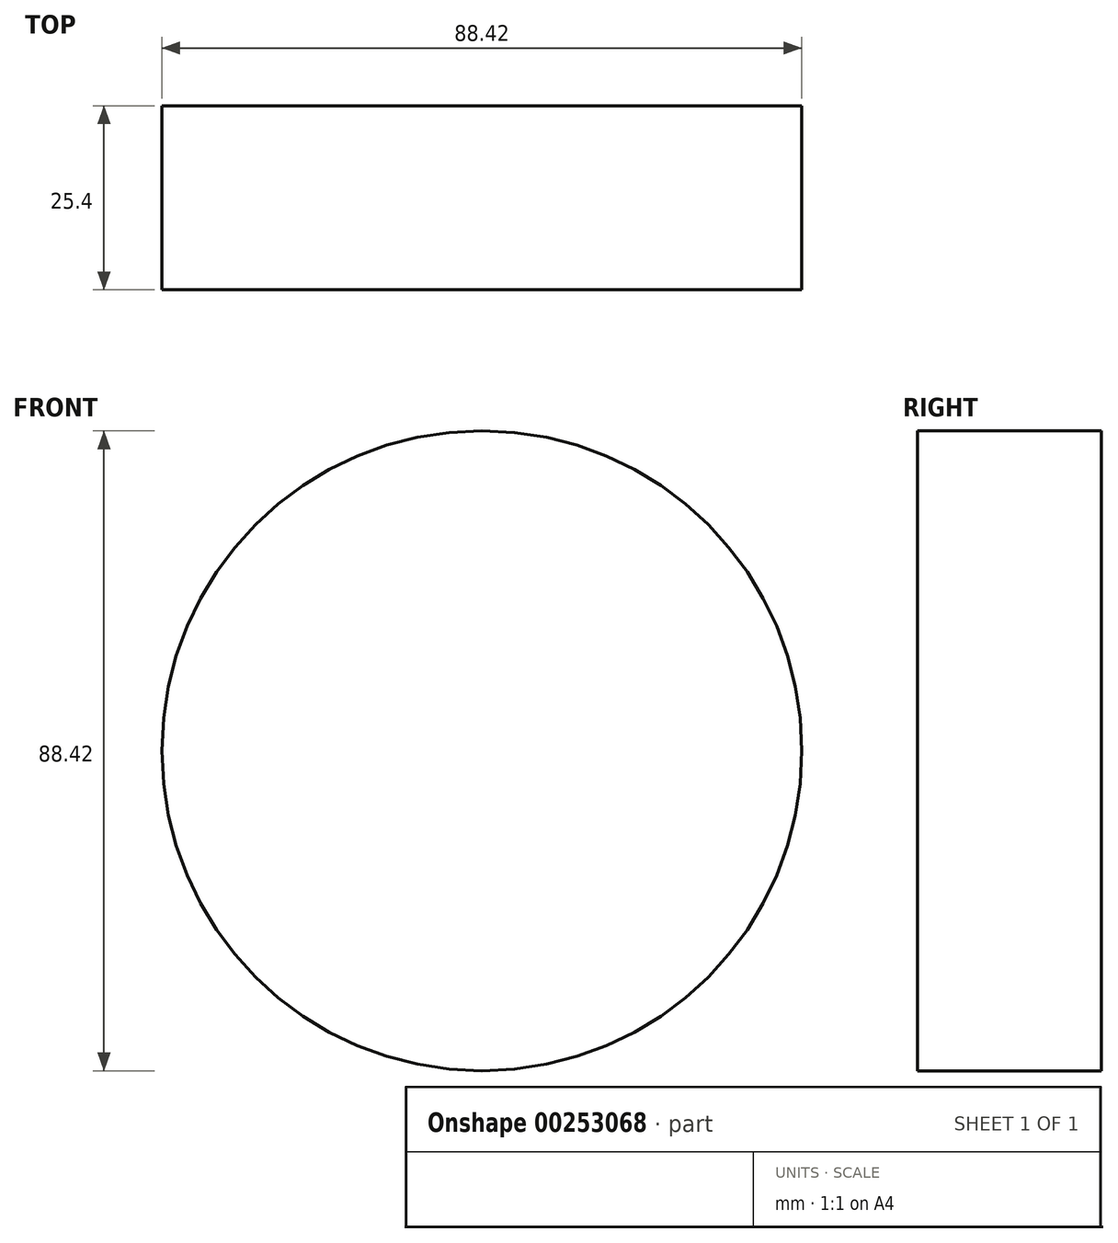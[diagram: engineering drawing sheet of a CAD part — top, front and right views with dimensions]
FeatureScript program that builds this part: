
annotation { "Feature Type Name" : "Feature", "Feature Type Description" : "" }
export const myFeature = defineFeature(function(context is Context, id is Id, definition is map)
    precondition{}
    {
        {
            var Q0;
            Q0=qCreatedBy(makeId("Front.planeOp"),FACE);
            var sketch = newSketch(context, id + "F0", { "sketchPlane" : qUnion([Q0])});
            skCircle(sketch, "E0", {"center": v(0, 0) * mm, "radius": 44.21 * mm});
            skSolve(sketch);
        }
        {
            var Q0;
            Q0 = qSketchRegion(id + "F0", true);
            extrude(context, id + "F1", {"entities" : qUnion([Q0]), "depth" : 25.4 * mm});
        }
    });
